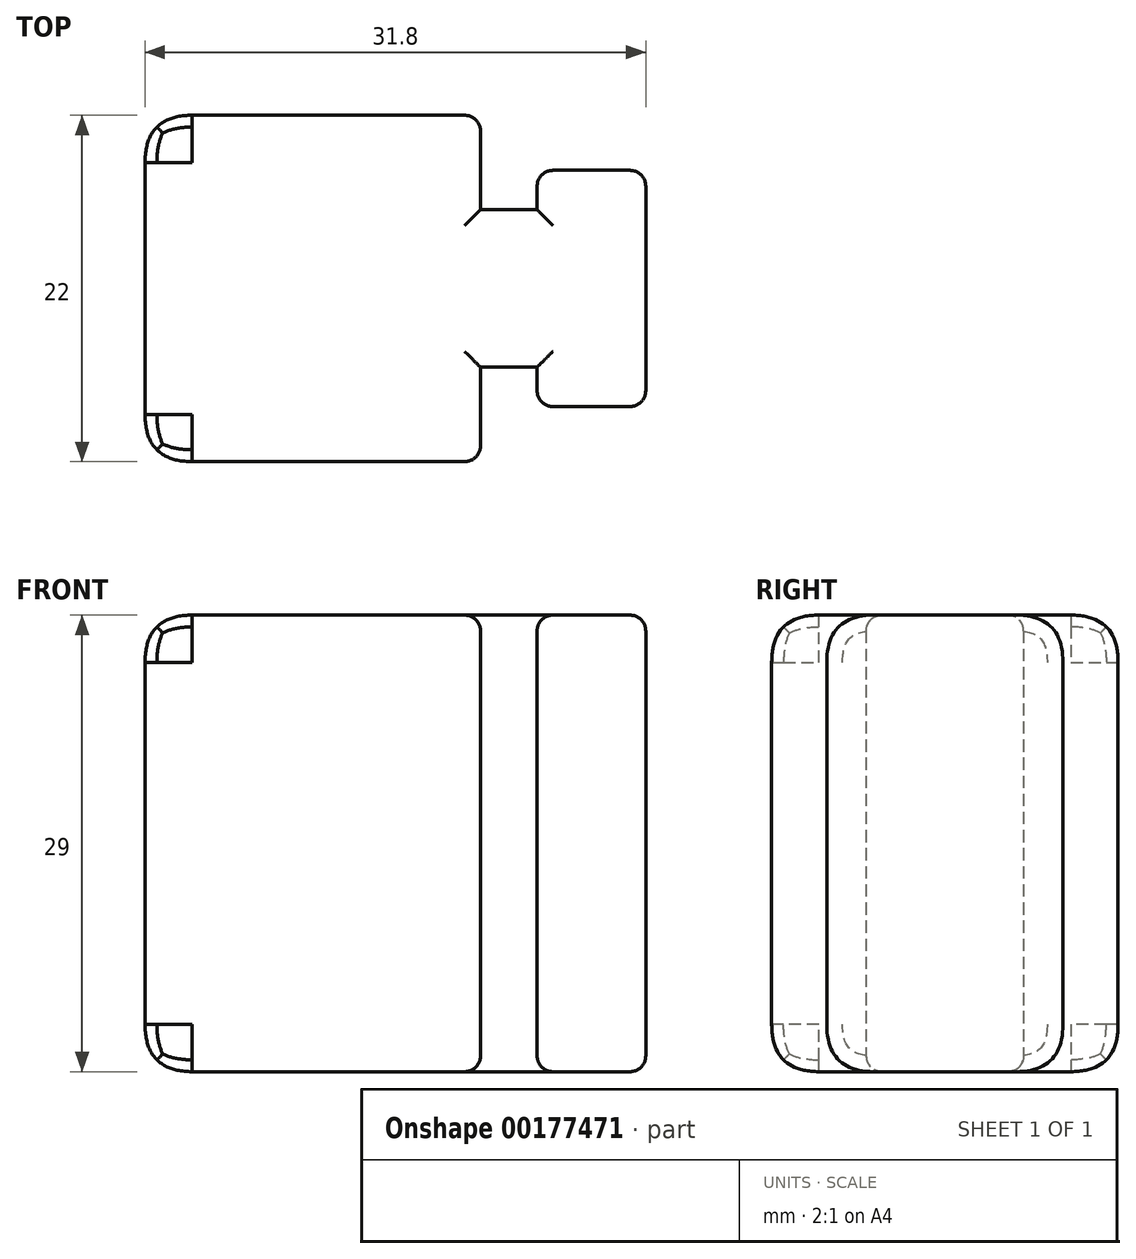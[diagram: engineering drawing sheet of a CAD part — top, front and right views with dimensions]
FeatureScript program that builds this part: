
annotation { "Feature Type Name" : "Feature", "Feature Type Description" : "" }
export const myFeature = defineFeature(function(context is Context, id is Id, definition is map)
    precondition{}
    {
        {
            var Q0;
            Q0=qCreatedBy(makeId("Top.planeOp"),FACE);
            var sketch = newSketch(context, id + "F0", { "sketchPlane" : qUnion([Q0])});
            skLineSegment(sketch, "E0.bottom", {"start": v(10.65, -11) * mm, "end": v(-10.65, -11) * mm});
            skLineSegment(sketch, "E0.top", {"start": v(10.65, 11) * mm, "end": v(-10.65, 11) * mm});
            skLineSegment(sketch, "E0.left", {"start": v(10.65, -11) * mm, "end": v(10.65, -5) * mm});
            skLineSegment(sketch, "E0.right", {"start": v(-10.65, -11) * mm, "end": v(-10.65, 11) * mm});
            skPoint(sketch, "E0.middle", {"position": v(0, 0) * mm});
            skLineSegment(sketch, "E1.bottom", {"start": v(14.25, -5) * mm, "end": v(10.65, -5) * mm});
            skLineSegment(sketch, "E1.top", {"start": v(14.25, 5) * mm, "end": v(10.65, 5) * mm});
            skPoint(sketch, "E1.middle", {"position": v(12.45, 0) * mm});
            skLineSegment(sketch, "E2.bottom", {"start": v(21.15, -7.5) * mm, "end": v(14.25, -7.5) * mm});
            skLineSegment(sketch, "E2.top", {"start": v(21.15, 7.5) * mm, "end": v(14.25, 7.5) * mm});
            skLineSegment(sketch, "E2.left", {"start": v(21.15, -7.5) * mm, "end": v(21.15, 7.5) * mm});
            skLineSegment(sketch, "E2.right", {"start": v(14.25, -7.5) * mm, "end": v(14.25, -5) * mm});
            skPoint(sketch, "E2.middle", {"position": v(17.7, 0) * mm});
            skLineSegment(sketch, "E3.trimOffspring", {"start": v(14.25, 5) * mm, "end": v(14.25, 7.5) * mm});
            skLineSegment(sketch, "E4.trimOffspring", {"start": v(10.65, 5) * mm, "end": v(10.65, 11) * mm});
            skSolve(sketch);
        }
        {
            var Q0;
            Q0 = qSketchRegion(id + "F0", true);
            extrude(context, id + "F1", {"entities" : qUnion([Q0]), "depth" : 29 * mm});
        }
        {
            var Q0;
            Q0=makeQuery(id+"F1.opExtrude","CAP_EDGE",EDGE,{"disambiguationData":[OSD([sQuery(id+"F0.wireOp",EDGE,"E0.bottom")])],"isStart":false});
            var Q1;
            Q1=makeQuery(id+"F1.opExtrude","CAP_EDGE",EDGE,{"disambiguationData":[OSD([sQuery(id+"F0.wireOp",EDGE,"E0.top")])],"isStart":false});
            var Q2;
            Q2=makeQuery(id+"F1.opExtrude","CAP_EDGE",EDGE,{"disambiguationData":[OSD([sQuery(id+"F0.wireOp",EDGE,"E0.right")])],"isStart":false});
            var Q3;
            Q3=makeQuery(id+"F1.opExtrude","SWEPT_EDGE",EDGE,{"disambiguationData":[OSD([sQuery(id+"F0.wireOp",EDGE,"E0.bottom"),sQuery(id+"F0.wireOp",EDGE,"E0.right")])]});
            var Q4;
            Q4=makeQuery(id+"F1.opExtrude","CAP_EDGE",EDGE,{"disambiguationData":[OSD([sQuery(id+"F0.wireOp",EDGE,"E0.bottom")])],"isStart":true});
            var Q5;
            Q5=makeQuery(id+"F1.opExtrude","CAP_EDGE",EDGE,{"disambiguationData":[OSD([sQuery(id+"F0.wireOp",EDGE,"E0.right")])],"isStart":true});
            var Q6;
            Q6=makeQuery(id+"F1.opExtrude","SWEPT_EDGE",EDGE,{"disambiguationData":[OSD([sQuery(id+"F0.wireOp",EDGE,"E0.top"),sQuery(id+"F0.wireOp",EDGE,"E0.right")])]});
            var Q7;
            Q7=makeQuery(id+"F1.opExtrude","CAP_EDGE",EDGE,{"disambiguationData":[OSD([sQuery(id+"F0.wireOp",EDGE,"E0.top")])],"isStart":true});
            var Q8;
            Q8=makeQuery(id+"F1.opExtrude","CAP_EDGE",EDGE,{"disambiguationData":[OSD([sQuery(id+"F0.wireOp",EDGE,"E2.bottom")])],"isStart":true});
            var Q9;
            Q9=makeQuery(id+"F1.opExtrude","CAP_EDGE",EDGE,{"disambiguationData":[OSD([sQuery(id+"F0.wireOp",EDGE,"E2.top")])],"isStart":true});
            var Q10;
            Q10=makeQuery(id+"F1.opExtrude","CAP_EDGE",EDGE,{"disambiguationData":[OSD([sQuery(id+"F0.wireOp",EDGE,"E2.bottom")])],"isStart":false});
            var Q11;
            Q11=makeQuery(id+"F1.opExtrude","CAP_EDGE",EDGE,{"disambiguationData":[OSD([sQuery(id+"F0.wireOp",EDGE,"E2.top")])],"isStart":false});
            fillet(context, id + "F2", {"entities" : qUnion([Q0, Q1, Q2, Q3, Q4, Q5, Q6, Q7, Q8, Q9, Q10, Q11]), "radius" : 3 * mm, "tangentPropagation" : true, "rho" : 0.5, "crossSection" : FilletCrossSection.CONIC, "allowEdgeOverflow" : false});
        }
        {
            var Q0;
            Q0=makeQuery(id+"F2.opFillet","BLEND_EDGE",EDGE,{"blendedFrom":[makeQuery(id+"F1.opExtrude","CAP_EDGE",EDGE,{"disambiguationData":[OSD([sQuery(id+"F0.wireOp",EDGE,"E2.bottom")])],"isStart":false}),makeQuery(id+"F1.opExtrude","SWEPT_FACE",FACE,{"disambiguationData":[OSD([sQuery(id+"F0.wireOp",EDGE,"E1.bottom")])]})],"blendedInto":[makeQuery(id+"F1.opExtrude","SWEPT_FACE",FACE,{"disambiguationData":[OSD([sQuery(id+"F0.wireOp",EDGE,"E1.bottom")])]})]});
            var Q1;
            Q1=makeQuery(id+"F2.opFillet","BLEND_EDGE",EDGE,{"blendedFrom":[makeQuery(id+"F1.opExtrude","CAP_EDGE",EDGE,{"disambiguationData":[OSD([sQuery(id+"F0.wireOp",EDGE,"E2.top")])],"isStart":false}),makeQuery(id+"F1.opExtrude","SWEPT_FACE",FACE,{"disambiguationData":[OSD([sQuery(id+"F0.wireOp",EDGE,"E1.top")])]})],"blendedInto":[makeQuery(id+"F1.opExtrude","SWEPT_FACE",FACE,{"disambiguationData":[OSD([sQuery(id+"F0.wireOp",EDGE,"E1.top")])]})]});
            var Q2;
            Q2=makeQuery(id+"F2.opFillet","BLEND_EDGE",EDGE,{"blendedFrom":[makeQuery(id+"F1.opExtrude","CAP_EDGE",EDGE,{"disambiguationData":[OSD([sQuery(id+"F0.wireOp",EDGE,"E2.bottom")])],"isStart":true}),makeQuery(id+"F1.opExtrude","SWEPT_FACE",FACE,{"disambiguationData":[OSD([sQuery(id+"F0.wireOp",EDGE,"E1.bottom")])]})],"blendedInto":[makeQuery(id+"F1.opExtrude","SWEPT_FACE",FACE,{"disambiguationData":[OSD([sQuery(id+"F0.wireOp",EDGE,"E1.bottom")])]})]});
            var Q3;
            Q3=makeQuery(id+"F2.opFillet","BLEND_EDGE",EDGE,{"blendedFrom":[makeQuery(id+"F1.opExtrude","CAP_EDGE",EDGE,{"disambiguationData":[OSD([sQuery(id+"F0.wireOp",EDGE,"E2.top")])],"isStart":true}),makeQuery(id+"F1.opExtrude","SWEPT_FACE",FACE,{"disambiguationData":[OSD([sQuery(id+"F0.wireOp",EDGE,"E1.top")])]})],"blendedInto":[makeQuery(id+"F1.opExtrude","SWEPT_FACE",FACE,{"disambiguationData":[OSD([sQuery(id+"F0.wireOp",EDGE,"E1.top")])]})]});
            var Q4;
            Q4=makeQuery(id+"F1.opExtrude","CAP_EDGE",EDGE,{"disambiguationData":[OSD([sQuery(id+"F0.wireOp",EDGE,"E4.trimOffspring")])],"isStart":true});
            var Q5;
            Q5=makeQuery(id+"F1.opExtrude","CAP_EDGE",EDGE,{"disambiguationData":[OSD([sQuery(id+"F0.wireOp",EDGE,"E0.left")])],"isStart":true});
            var Q6;
            Q6=makeQuery(id+"F2.opFillet","BLEND_EDGE",EDGE,{"blendedFrom":[makeQuery(id+"F1.opExtrude","CAP_EDGE",EDGE,{"disambiguationData":[OSD([sQuery(id+"F0.wireOp",EDGE,"E2.top")])],"isStart":true}),makeQuery(id+"F1.opExtrude","SWEPT_FACE",FACE,{"disambiguationData":[OSD([sQuery(id+"F0.wireOp",EDGE,"E3.trimOffspring")])]})],"blendedInto":[makeQuery(id+"F1.opExtrude","SWEPT_FACE",FACE,{"disambiguationData":[OSD([sQuery(id+"F0.wireOp",EDGE,"E3.trimOffspring")])]})]});
            var Q7;
            Q7=makeQuery(id+"F2.opFillet","BLEND_EDGE",EDGE,{"blendedFrom":[makeQuery(id+"F1.opExtrude","CAP_EDGE",EDGE,{"disambiguationData":[OSD([sQuery(id+"F0.wireOp",EDGE,"E2.bottom")])],"isStart":true}),makeQuery(id+"F1.opExtrude","SWEPT_FACE",FACE,{"disambiguationData":[OSD([sQuery(id+"F0.wireOp",EDGE,"E2.right")])]})],"blendedInto":[makeQuery(id+"F1.opExtrude","SWEPT_FACE",FACE,{"disambiguationData":[OSD([sQuery(id+"F0.wireOp",EDGE,"E2.right")])]})]});
            var Q8;
            Q8=makeQuery(id+"F1.opExtrude","CAP_EDGE",EDGE,{"disambiguationData":[OSD([sQuery(id+"F0.wireOp",EDGE,"E2.left")])],"isStart":true});
            fillet(context, id + "F3", {"entities" : qUnion([Q0, Q1, Q2, Q3, Q4, Q5, Q6, Q7, Q8]), "radius" : 1 * mm, "tangentPropagation" : true, "allowEdgeOverflow" : false});
        }
    });
